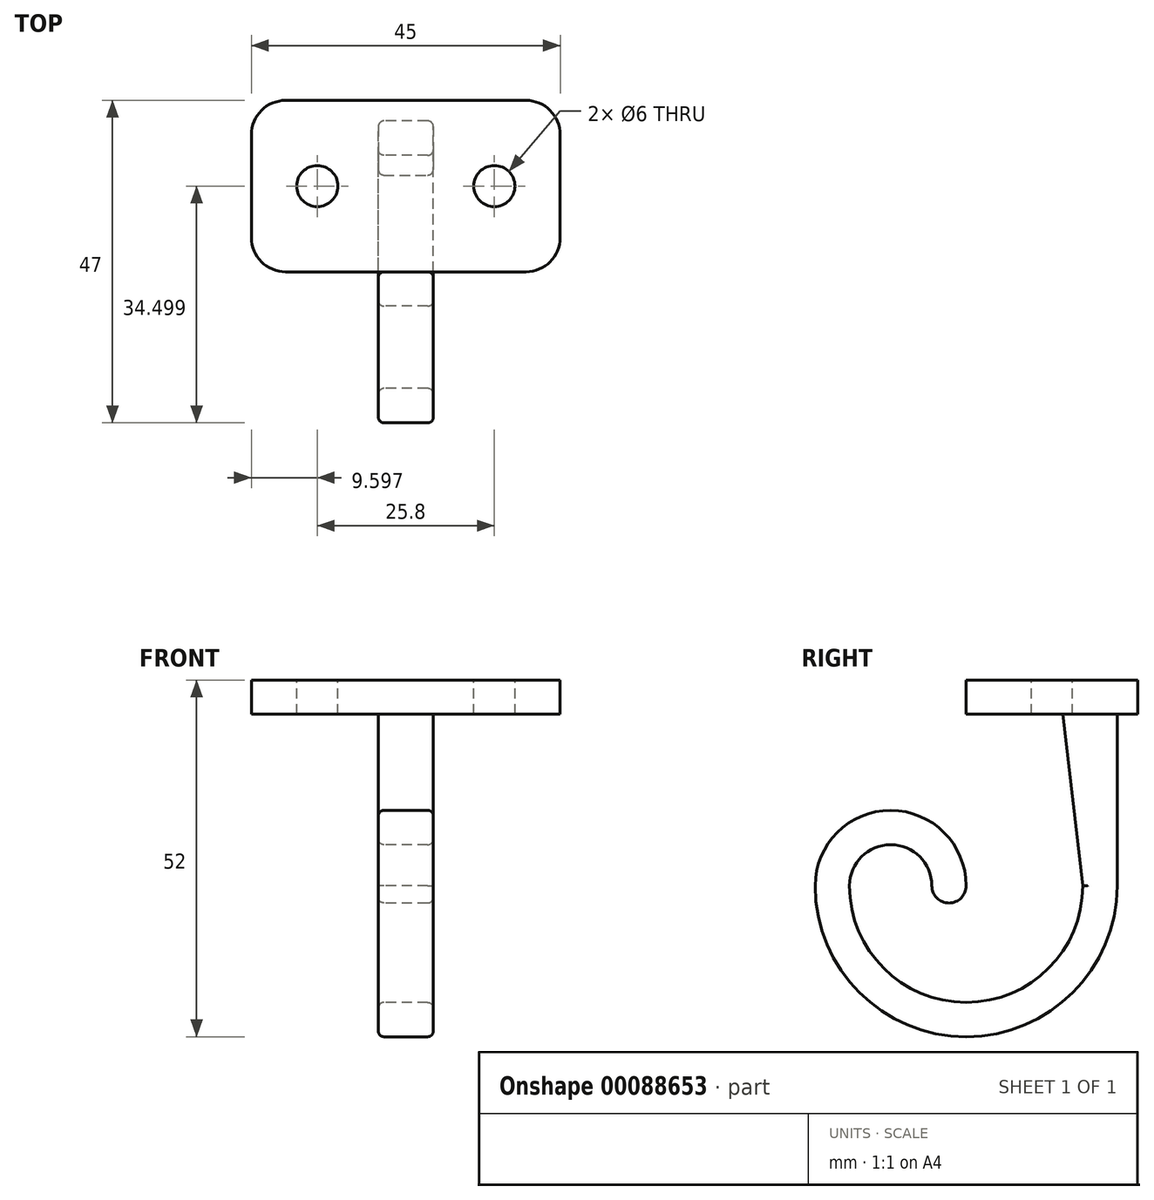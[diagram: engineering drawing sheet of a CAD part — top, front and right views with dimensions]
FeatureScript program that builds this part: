
annotation { "Feature Type Name" : "Feature", "Feature Type Description" : "" }
export const myFeature = defineFeature(function(context is Context, id is Id, definition is map)
    precondition{}
    {
        {
            var Q0;
            Q0=qCreatedBy(makeId("Top.planeOp"),FACE);
            var sketch = newSketch(context, id + "F0", { "sketchPlane" : qUnion([Q0])});
            skLineSegment(sketch, "E0.bottom", {"start": v(-33.86, 18.59) * mm, "end": v(11.14, 18.59) * mm});
            skLineSegment(sketch, "E0.top", {"start": v(-33.86, -6.41) * mm, "end": v(11.14, -6.41) * mm});
            skLineSegment(sketch, "E0.left", {"start": v(-33.86, 18.59) * mm, "end": v(-33.86, -6.41) * mm});
            skLineSegment(sketch, "E0.right", {"start": v(11.14, 18.59) * mm, "end": v(11.14, -6.41) * mm});
            skLineSegment(sketch, "E1", {"start": v(-11.36, 18.59) * mm, "end": v(-11.36, -6.41) * mm, "construction": true});
            skSolve(sketch);
        }
        {
            var Q0;
            Q0=makeQuery(id+"F0.imprint","IMPRINT",FACE,{"disambiguationData":[TD([[makeQuery(id+"F0.imprint","IMPRINT",EDGE,{"derivedFrom":sQuery(id+"F0.wireOp",EDGE,"E0.bottom")}),-1.0]])]});
            extrude(context, id + "F1", {"entities" : qUnion([Q0]), "depth" : 5 * mm});
        }
        {
            var Q0;
            Q0=makeQuery(id+"F1.opExtrude","CAP_FACE",FACE,{"disambiguationData":[OSD([sQuery(id+"F0.wireOp",EDGE,"E0.bottom"),sQuery(id+"F0.wireOp",EDGE,"E0.top"),sQuery(id+"F0.wireOp",EDGE,"E0.left"),sQuery(id+"F0.wireOp",EDGE,"E0.right")])],"isStart":false});
            var sketch = newSketch(context, id + "F2", { "sketchPlane" : qUnion([Q0])});
            skCircle(sketch, "E2", {"center": v(-24.26, 6.09) * mm, "radius": 3 * mm});
            skCircle(sketch, "E3", {"center": v(1.54, 6.09) * mm, "radius": 3 * mm});
            skLineSegment(sketch, "E4", {"start": v(-33.86, 6.09) * mm, "end": v(11.14, 6.09) * mm, "construction": true});
            skLineSegment(sketch, "E5", {"start": v(-33.86, -1.29) * mm, "end": v(-24.26, -1.29) * mm, "construction": true});
            skLineSegment(sketch, "E6", {"start": v(-24.26, -1.29) * mm, "end": v(-24.26, 6.09) * mm, "construction": true});
            skLineSegment(sketch, "E7", {"start": v(11.14, -1.14) * mm, "end": v(1.54, -1.14) * mm, "construction": true});
            skLineSegment(sketch, "E8", {"start": v(1.54, -1.14) * mm, "end": v(1.54, 6.09) * mm, "construction": true});
            skSolve(sketch);
        }
        {
            var Q0;
            Q0 = qSketchRegion(id + "F2", true);
            extrude(context, id + "F3", {"entities" : qUnion([Q0]), "operationType" : NewBodyOperationType.REMOVE, "oppositeDirection" : true, "depth" : 25 * mm});
        }
        {
            var Q0;
            Q0=sQuery(id+"F0.wireOp",EDGE,"E1");
            cPlane(context, id + "F4", {"entities" : qUnion([Q0]), "cplaneType" : CPlaneType.LINE_ANGLE, "offset" : 150 * mm, "angle" : 90 * degree, "width" : 150 * mm, "height" : 150 * mm});
        }
        {
            var Q0;
            Q0=qCreatedBy(id+"F4.planeOp",FACE);
            var sketch = newSketch(context, id + "F5", { "sketchPlane" : qUnion([Q0])});
            skLineSegment(sketch, "E9.0", {"start": v(18.59, 0) * mm, "end": v(-6.41, 0) * mm});
            skLineSegment(sketch, "E10", {"start": v(15.59, 0) * mm, "end": v(15.59, -25) * mm});
            skArc(sketch, "E11", {"start": v(-28.41, -25) * mm, "mid": v(-6.41, -47) * mm, "end": v(15.59, -25) * mm});
            skArc(sketch, "E12", {"start": v(-6.41, -25) * mm, "mid": v(-17.41, -14) * mm, "end": v(-28.41, -25) * mm});
            skArc(sketch, "E13.0", {"start": v(-23.41, -25) * mm, "mid": v(-6.41, -42) * mm, "end": v(10.59, -25) * mm});
            skLineSegment(sketch, "E13.1", {"start": v(10.59, 0) * mm, "end": v(10.59, -25) * mm});
            skArc(sketch, "E14.0", {"start": v(-11.41, -25) * mm, "mid": v(-17.41, -19) * mm, "end": v(-23.41, -25) * mm});
            skArc(sketch, "E15", {"start": v(-11.41, -25) * mm, "mid": v(-8.91, -27.5) * mm, "end": v(-6.41, -25) * mm});
            skLineSegment(sketch, "E16", {"start": v(15.59, 0) * mm, "end": v(18.59, 0) * mm});
            skLineSegment(sketch, "E17", {"start": v(-23.41, -25) * mm, "end": v(-28.41, -25) * mm, "construction": true});
            skSolve(sketch);
        }
        {
            var Q0;
            {var subQ0=sQuery(id+"F5.wireOp",EDGE,"E10");Q0=makeQuery(id+"F5.imprint","IMPRINT",FACE,{"disambiguationData":[TD([[makeQuery(id+"F5.imprint","IMPRINT",EDGE,{"derivedFrom":subQ0}),-1.0]])]});}
            extrude(context, id + "F6", {"entities" : qUnion([Q0]), "operationType" : NewBodyOperationType.ADD, "endBound" : BoundingType.SYMMETRIC, "depth" : 8 * mm});
        }
        {
            var Q0;
            Q0=makeQuery(id+"F0.imprint","IMPRINT",FACE,{"disambiguationData":[TD([[makeQuery(id+"F0.imprint","IMPRINT",EDGE,{"derivedFrom":sQuery(id+"F0.wireOp",EDGE,"E0.bottom")}),-1.0]])]});
            var sketch = newSketch(context, id + "F7", { "sketchPlane" : qUnion([Q0])});
            skLineSegment(sketch, "E18.0.0", {"start": v(11.14, 18.59) * mm, "end": v(-33.86, 18.59) * mm});
            skLineSegment(sketch, "E18.0.1", {"start": v(-33.86, 18.59) * mm, "end": v(-33.86, -6.41) * mm});
            skLineSegment(sketch, "E18.0.2", {"start": v(-33.86, -6.41) * mm, "end": v(11.14, -6.41) * mm});
            skLineSegment(sketch, "E18.0.3", {"start": v(11.14, -6.41) * mm, "end": v(11.14, 18.59) * mm});
            skLineSegment(sketch, "E19", {"start": v(-15.36, 7.7) * mm, "end": v(-7.36, 7.7) * mm});
            skLineSegment(sketch, "E20.1", {"start": v(-7.36, 15.59) * mm, "end": v(-15.36, 15.59) * mm});
            skLineSegment(sketch, "E21", {"start": v(-7.36, 7.7) * mm, "end": v(-7.36, 15.59) * mm});
            skLineSegment(sketch, "E22", {"start": v(-15.36, 7.7) * mm, "end": v(-15.36, 15.59) * mm});
            skSolve(sketch);
        }
        {
            var Q0;
            Q0=makeQuery(id+"F6.opExtrude","SWEPT_EDGE",EDGE,{"disambiguationData":[OSD([sQuery(id+"F5.wireOp",EDGE,"E13.0"),sQuery(id+"F5.wireOp",EDGE,"E13.1")])]});
            cPlane(context, id + "F8", {"entities" : qUnion([Q0]), "cplaneType" : CPlaneType.LINE_ANGLE, "offset" : 150 * mm, "angle" : 90 * degree, "width" : 150 * mm, "height" : 150 * mm});
        }
        {
            var Q0;
            Q0=qCreatedBy(id+"F8.planeOp",FACE);
            var sketch = newSketch(context, id + "F9", { "sketchPlane" : qUnion([Q0])});
            skPoint(sketch, "E23.0", {"position": v(-7.36, 15.59) * mm});
            skPoint(sketch, "E23.1", {"position": v(-7.36, 10.59) * mm});
            skPoint(sketch, "E23.2", {"position": v(-15.36, 15.59) * mm});
            skPoint(sketch, "E23.3", {"position": v(-15.36, 10.59) * mm});
            skLineSegment(sketch, "E24", {"start": v(-15.36, 10.59) * mm, "end": v(-15.36, 15.59) * mm});
            skLineSegment(sketch, "E25", {"start": v(-7.36, 15.59) * mm, "end": v(-7.36, 10.59) * mm});
            skLineSegment(sketch, "E26", {"start": v(-7.36, 10.59) * mm, "end": v(-15.36, 10.59) * mm});
            skLineSegment(sketch, "E27", {"start": v(-7.36, 15.59) * mm, "end": v(-15.36, 15.59) * mm});
            skSolve(sketch);
        }
        {
            var Q1;
            Q1=makeQuery(id+"F7.imprint","IMPRINT",FACE,{"disambiguationData":[TD([[makeQuery(id+"F7.imprint","IMPRINT",EDGE,{"derivedFrom":sQuery(id+"F7.wireOp",EDGE,"E19")}),1.0]])]});
            var Q2;
            Q2=makeQuery(id+"F9.imprint","IMPRINT",FACE,{"disambiguationData":[TD([[makeQuery(id+"F9.imprint","IMPRINT",EDGE,{"derivedFrom":sQuery(id+"F9.wireOp",EDGE,"E24")}),-1.0]])]});
            loft(context, id + "F10", {"operationType" : NewBodyOperationType.ADD, "sheetProfilesArray" : [{ "sheetProfileEntities" : qUnion([Q1]) }, { "sheetProfileEntities" : qUnion([Q2]) }]});
        }
        {
            var Q0;
            Q0=makeQuery(id+"F1.opExtrude","SWEPT_EDGE",EDGE,{"disambiguationData":[OSD([sQuery(id+"F0.wireOp",EDGE,"E0.bottom"),sQuery(id+"F0.wireOp",EDGE,"E0.left")])]});
            var Q1;
            Q1=makeQuery(id+"F1.opExtrude","SWEPT_EDGE",EDGE,{"disambiguationData":[OSD([sQuery(id+"F0.wireOp",EDGE,"E0.top"),sQuery(id+"F0.wireOp",EDGE,"E0.left")])]});
            var Q2;
            Q2=makeQuery(id+"F1.opExtrude","SWEPT_EDGE",EDGE,{"disambiguationData":[OSD([sQuery(id+"F0.wireOp",EDGE,"E0.bottom"),sQuery(id+"F0.wireOp",EDGE,"E0.right")])]});
            var Q3;
            Q3=makeQuery(id+"F1.opExtrude","SWEPT_EDGE",EDGE,{"disambiguationData":[OSD([sQuery(id+"F0.wireOp",EDGE,"E0.top"),sQuery(id+"F0.wireOp",EDGE,"E0.right")])]});
            fillet(context, id + "F11", {"entities" : qUnion([Q0, Q1, Q2, Q3]), "radius" : 5 * mm, "tangentPropagation" : true, "allowEdgeOverflow" : false});
        }
        {
            var Q0;
            Q0=makeQuery(id+"F6.opExtrude","CAP_EDGE",EDGE,{"disambiguationData":[OSD([sQuery(id+"F5.wireOp",EDGE,"E10")])],"isStart":false});
            var Q1;
            Q1=makeQuery(id+"F6.opExtrude","CAP_EDGE",EDGE,{"disambiguationData":[OSD([sQuery(id+"F5.wireOp",EDGE,"E11")])],"isStart":false});
            var Q2;
            Q2=makeQuery(id+"F6.opExtrude","CAP_EDGE",EDGE,{"disambiguationData":[OSD([sQuery(id+"F5.wireOp",EDGE,"E10")])],"isStart":true});
            var Q3;
            Q3=makeQuery(id+"F6.opExtrude","CAP_EDGE",EDGE,{"disambiguationData":[OSD([sQuery(id+"F5.wireOp",EDGE,"E11")])],"isStart":true});
            var Q4;
            Q4=makeQuery(id+"F10.opLoft","SWEPT_EDGE",EDGE,{"disambiguationData":[OSD([sQuery(id+"F7.wireOp",EDGE,"E19"),sQuery(id+"F7.wireOp",EDGE,"E22"),sQuery(id+"F9.wireOp",EDGE,"E24"),sQuery(id+"F9.wireOp",EDGE,"E26")])]});
            var Q5;
            Q5=makeQuery(id+"F10.opLoft","SWEPT_EDGE",EDGE,{"disambiguationData":[OSD([sQuery(id+"F7.wireOp",EDGE,"E19"),sQuery(id+"F7.wireOp",EDGE,"E21"),sQuery(id+"F9.wireOp",EDGE,"E25"),sQuery(id+"F9.wireOp",EDGE,"E26")])]});
            fillet(context, id + "F12", {"entities" : qUnion([Q0, Q1, Q2, Q3, Q4, Q5]), "radius" : .8 * mm, "tangentPropagation" : true, "allowEdgeOverflow" : false});
        }
    });
